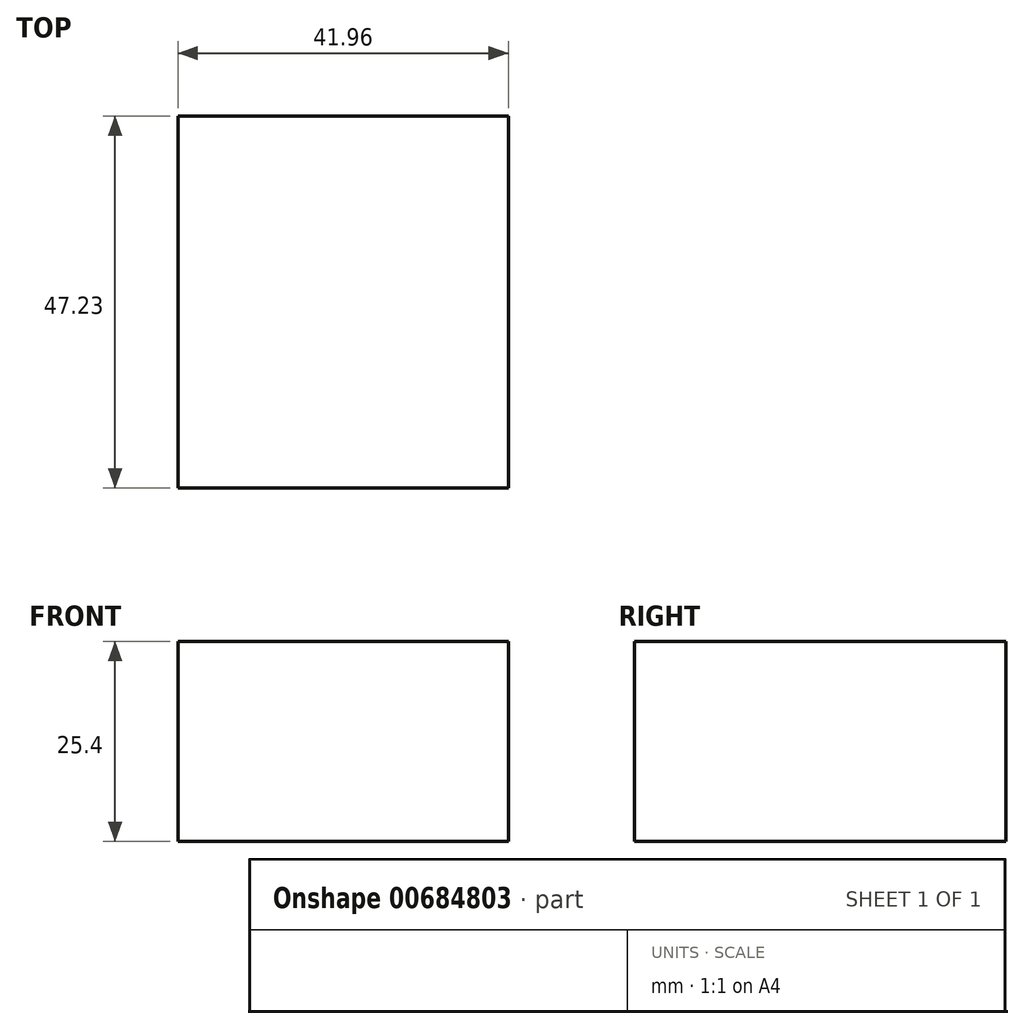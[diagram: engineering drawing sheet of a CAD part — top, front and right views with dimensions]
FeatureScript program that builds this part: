
annotation { "Feature Type Name" : "Feature", "Feature Type Description" : "" }
export const myFeature = defineFeature(function(context is Context, id is Id, definition is map)
    precondition{}
    {
        {
            var Q0;
            Q0=qCreatedBy(makeId("Top.planeOp"),FACE);
            var sketch = newSketch(context, id + "F0", { "sketchPlane" : qUnion([Q0])});
            skLineSegment(sketch, "E0.bottom", {"start": v(41.96, 47.23) * mm, "end": v(0, 47.23) * mm});
            skLineSegment(sketch, "E0.top", {"start": v(41.96, 0) * mm, "end": v(0, 0) * mm});
            skLineSegment(sketch, "E0.left", {"start": v(41.96, 47.23) * mm, "end": v(41.96, 0) * mm});
            skLineSegment(sketch, "E0.right", {"start": v(0, 47.23) * mm, "end": v(0, 0) * mm});
            skSolve(sketch);
        }
        {
            var Q0;
            Q0=makeQuery(id+"F0.imprint","IMPRINT",FACE,{"disambiguationData":[TD([[makeQuery(id+"F0.imprint","IMPRINT",EDGE,{"derivedFrom":sQuery(id+"F0.wireOp",EDGE,"E0.bottom")}),1.0]])]});
            var Q1;
            Q1=sQuery(id+"F0.wireOp",EDGE,"E0.left");
            var Q2;
            Q2=sQuery(id+"F0.wireOp",EDGE,"E0.top");
            var Q3;
            Q3=sQuery(id+"F0.wireOp",EDGE,"E0.bottom");
            var Q4;
            Q4=sQuery(id+"F0.wireOp",EDGE,"E0.right");
            extrude(context, id + "F1", {"entities" : qUnion([Q0]), "surfaceEntities" : qUnion([Q1, Q2, Q3, Q4]), "depth" : 25.4 * mm, "offsetDistance" : 25.4 * mm});
        }
    });
